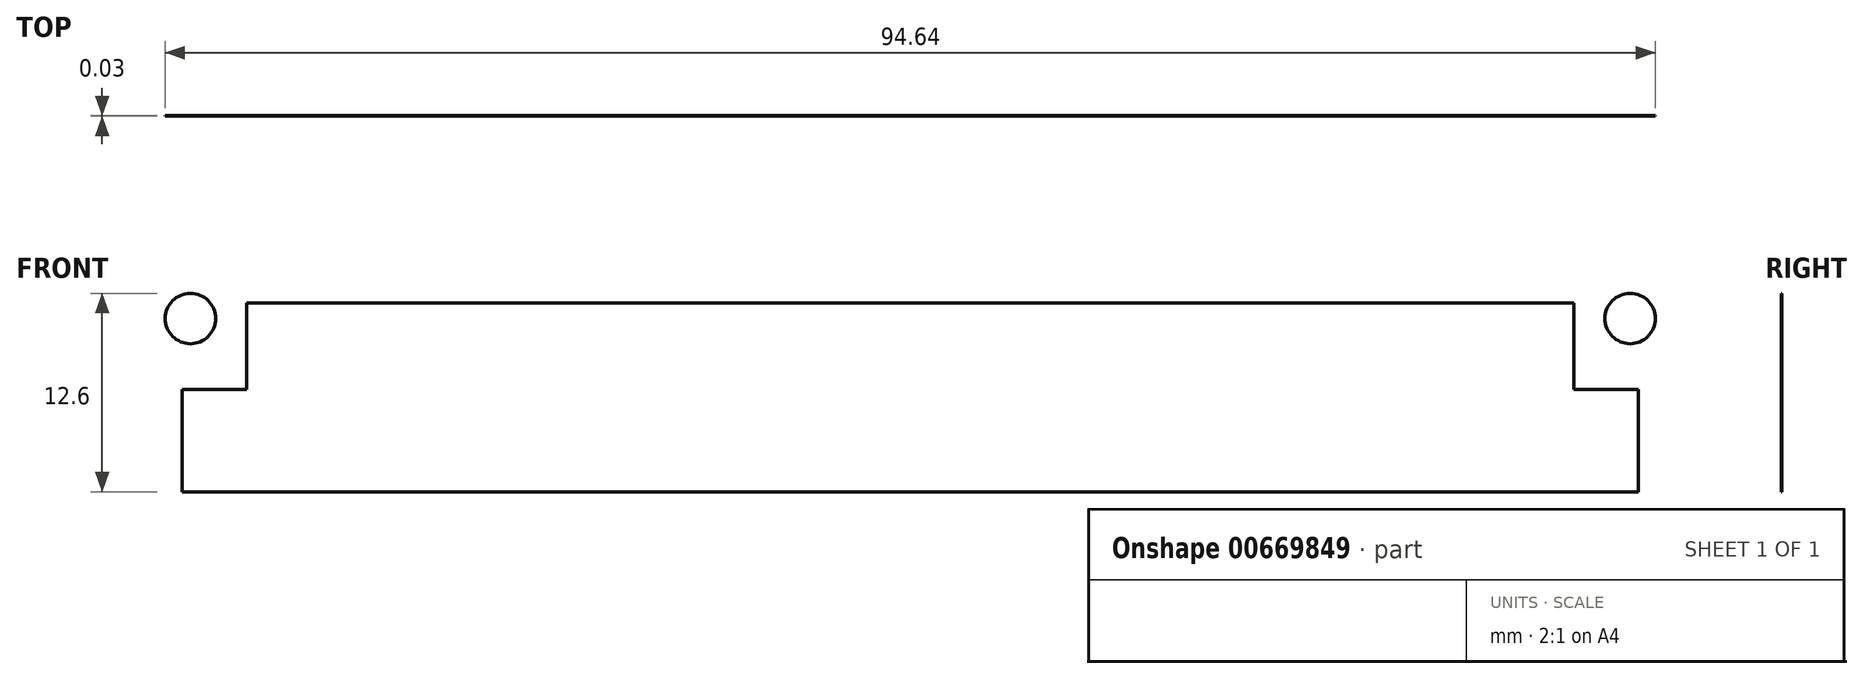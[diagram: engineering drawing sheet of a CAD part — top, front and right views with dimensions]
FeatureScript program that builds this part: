
annotation { "Feature Type Name" : "Feature", "Feature Type Description" : "" }
export const myFeature = defineFeature(function(context is Context, id is Id, definition is map)
    precondition{}
    {
        {
            var Q0;
            Q0=qCreatedBy(makeId("Front.planeOp"),FACE);
            var sketch = newSketch(context, id + "F0", { "sketchPlane" : qUnion([Q0])});
            skLineSegment(sketch, "E0.bottom", {"start": v(0, 0) * mm, "end": v(92.5, 0) * mm});
            skLineSegment(sketch, "E0.top", {"start": v(0, 6.5) * mm, "end": v(92.5, 6.5) * mm});
            skLineSegment(sketch, "E0.left", {"start": v(0, 0) * mm, "end": v(0, 6.5) * mm});
            skLineSegment(sketch, "E0.right", {"start": v(92.5, 0) * mm, "end": v(92.5, 6.5) * mm});
            skLineSegment(sketch, "E1.bottom", {"start": v(4.1, 6.5) * mm, "end": v(88.4, 6.5) * mm});
            skLineSegment(sketch, "E1.top", {"start": v(4.1, 12) * mm, "end": v(88.4, 12) * mm});
            skLineSegment(sketch, "E1.left", {"start": v(88.4, 6.5) * mm, "end": v(88.4, 12) * mm});
            skLineSegment(sketch, "E1.right", {"start": v(4.1, 6.5) * mm, "end": v(4.1, 12) * mm});
            skLineSegment(sketch, "E2", {"start": v(46.25, 0) * mm, "end": v(46.25, 12) * mm, "construction": true});
            skCircle(sketch, "E3", {"center": v(0.53, 11) * mm, "radius": 1.6 * mm});
            skCircle(sketch, "E4", {"center": v(91.97, 11) * mm, "radius": 1.6 * mm});
            skLineSegment(sketch, "E5", {"start": v(0.53, 11) * mm, "end": v(91.97, 11) * mm, "construction": true});
            skSolve(sketch);
        }
        {
            var Q0;
            Q0=qSketchRegion(id+"F0",true);
            extrude(context, id + "F1", {"entities" : qUnion([Q0]), "depth" : 0.03 * mm, "offsetDistance" : 25.4 * mm});
        }
    });
